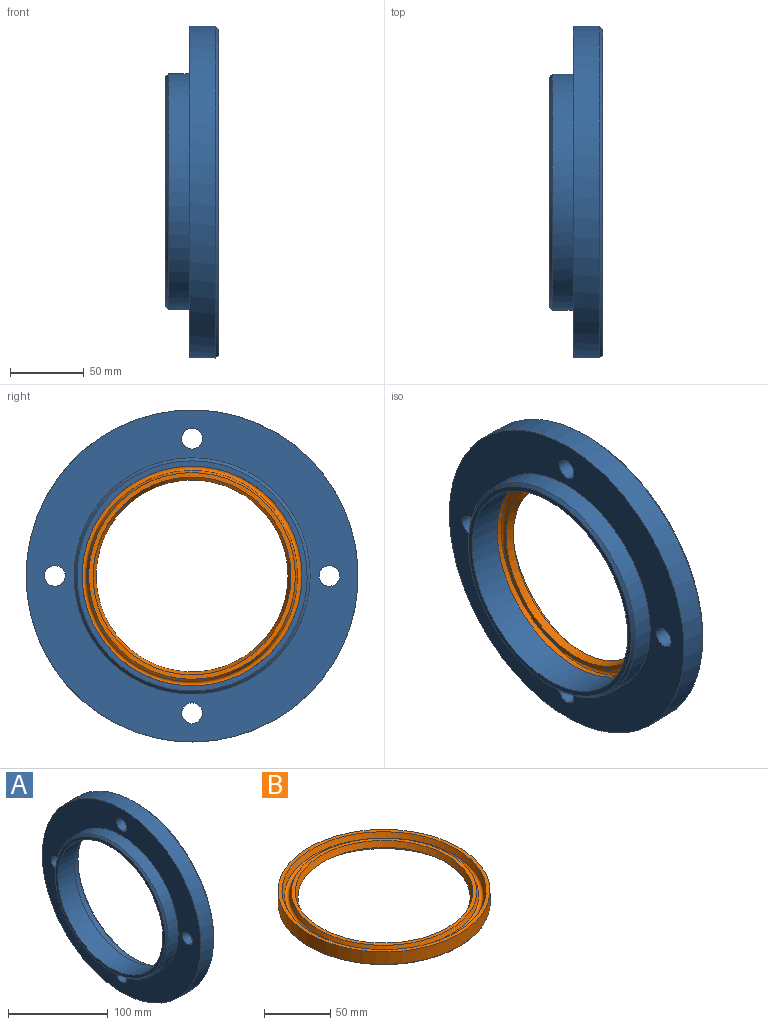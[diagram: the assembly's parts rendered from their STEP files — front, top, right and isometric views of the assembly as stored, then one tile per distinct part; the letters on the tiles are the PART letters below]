
ASSEMBLY  parts=2 mates=1
PART A: 15 faces, bbox 36x225x225 mm
  f0: cylinder r=74.5mm len=149mm, axis (-1,0,0), area 11234.3mm2, adj f5,f12
  f1: plane 221x221mm, normal (1,0,0), area 16619.8mm2, adj f7,f8,f9,f10,f11,f14
  f2: cylinder r=112.5mm len=225mm, axis (-1,0,0), area 12652.8mm2, adj f3,f11
  f3: plane 225x225mm, normal (-1,0,0), area 19038.8mm2, adj f2,f4,f7,f8,f9,f10
  f4: cylinder r=80mm len=160mm, axis (1,0,0), area 7087.4mm2, adj f3,f6
  f5: plane 156x156mm, normal (-1,0,0), area 1676.8mm2, adj f0,f6
  f6: cone r=78mm half-angle=45deg, axis (1,0,0), area 1404mm2, adj f4,f5
  f7: cylinder r=7mm len=19.9mm, axis (1,0,0), area 875.2mm2, adj f1,f3
  f8: cylinder r=7mm len=19.9mm, axis (1,0,0), area 875.2mm2, adj f1,f3
  f9: cylinder r=7mm len=19.9mm, axis (1,0,0), area 875.2mm2, adj f1,f3
  f10: cylinder r=7mm len=19.9mm, axis (1,0,0), area 875.2mm2, adj f1,f3
  f11: cone r=110.5mm half-angle=45deg, axis (-1,0,0), area 1981.5mm2, adj f1,f2
  f12: plane 160x160mm, normal (1,0,0), area 2669.6mm2, adj f0,f13
  f13: cylinder r=80mm len=160mm, axis (1,0,0), area 5026.5mm2, adj f12,f14
  f14: cone r=80mm half-angle=45deg, axis (1,0,0), area 1439.5mm2, adj f1,f13
PART B: 13 faces, bbox 173.2x173.2x12 mm
  f0: cone r=77mm half-angle=22.5deg, axis (0,0,1), area 2322.3mm2, adj f1,f10
  f1: plane 160x160mm, normal (0,0,1), area 1479.7mm2, adj f0,f2
  f2: cylinder r=80mm len=160mm, axis (0,0,1), area 5780.5mm2, adj f1,f12
  f3: plane 159x159mm, normal (0,0,-1), area 3569.6mm2, adj f4,f12
  f4: cone r=71.29mm half-angle=10deg, axis (0,0,-1), area 1640.4mm2, adj f3,f11
  f5: plane 141.75x141.75mm, normal (0,0,-1), area 387.3mm2, adj f6,f11
  f6: cone r=65mm half-angle=68.2deg, axis (0,0,-1), area 2283.9mm2, adj f5,f7
  f7: cone r=67mm half-angle=21.8deg, axis (0,0,1), area 2233.2mm2, adj f6,f8
  f8: plane 140x140mm, normal (0,0,1), area 1291.2mm2, adj f7,f9
  f9: cone r=71.45mm half-angle=22.5deg, axis (0,0,-1), area 1678.1mm2, adj f8,f10
  f10: torus R=73.29mm, axis (0,0,1), area 2170.1mm2, adj f0,f9
  f11: torus R=70.88mm, axis (0,0,1), area 312.2mm2, adj f4,f5
  f12: torus R=79.5mm, axis (0,0,1), area 393.9mm2, adj f2,f3
PLACE A at identity
PLACE B rot(axis=(0,-1,0),90deg) t=(19.9,0,0)mm
MATE fastened B.f0 <-> A.f0  axis (1,0,0) through (19.9,0,0)mm
